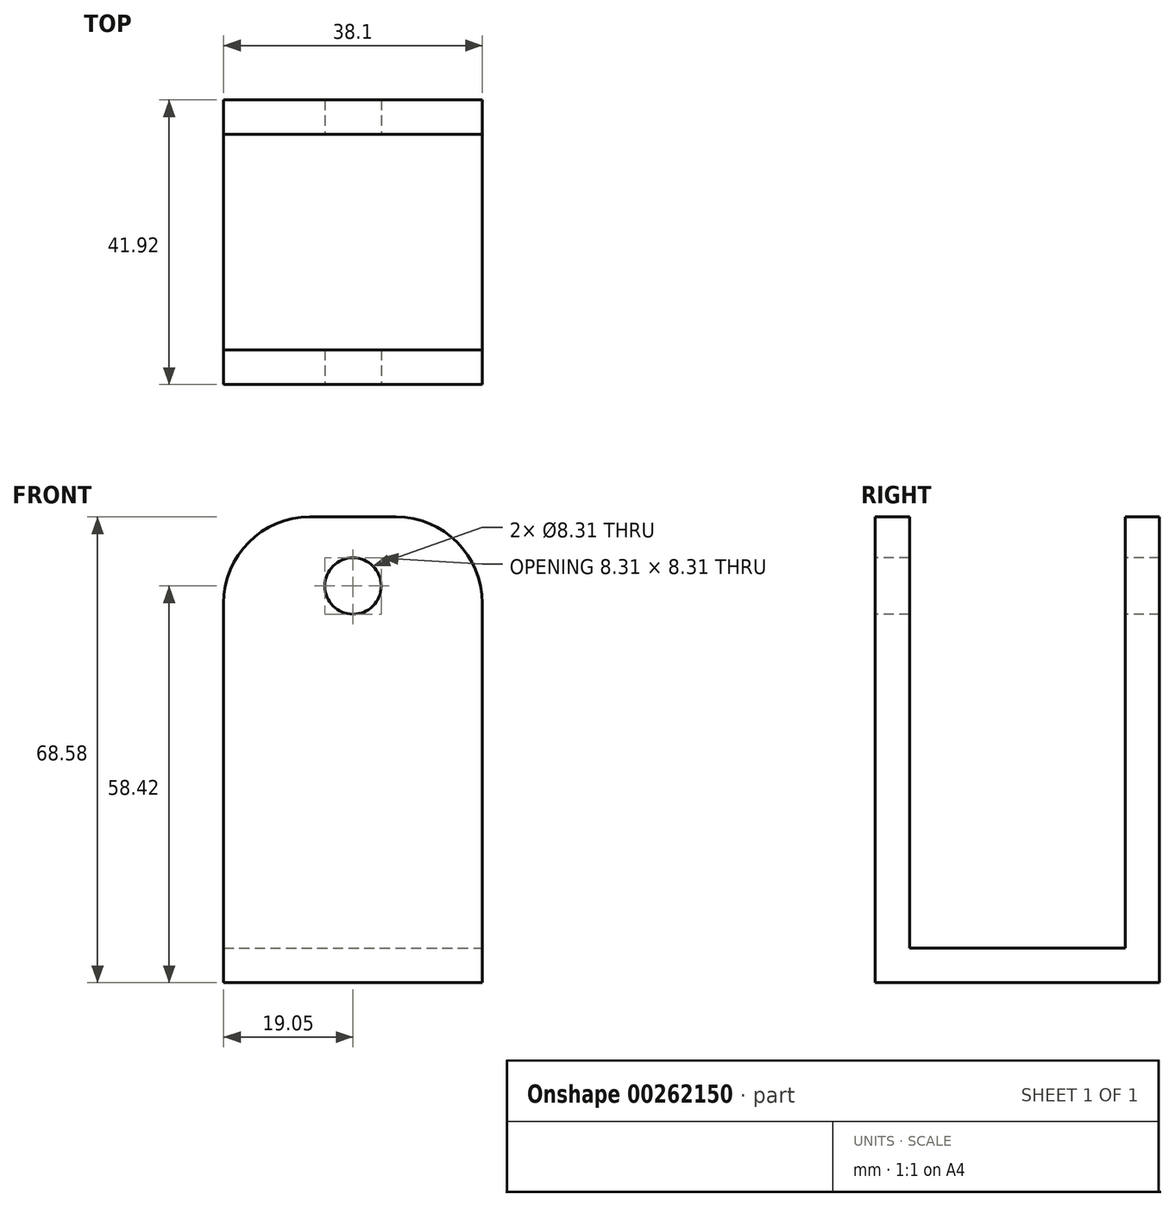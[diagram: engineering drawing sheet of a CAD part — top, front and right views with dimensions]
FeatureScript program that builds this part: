
annotation { "Feature Type Name" : "Feature", "Feature Type Description" : "" }
export const myFeature = defineFeature(function(context is Context, id is Id, definition is map)
    precondition{}
    {
        {
            var Q0;
            Q0=qCreatedBy(makeId("Top.planeOp"),FACE);
            var sketch = newSketch(context, id + "F0", { "sketchPlane" : qUnion([Q0])});
            skLineSegment(sketch, "E0.bottom", {"start": v(19.05, 20.95) * mm, "end": v(-19.05, 20.95) * mm});
            skLineSegment(sketch, "E0.top", {"start": v(19.05, -20.96) * mm, "end": v(-19.05, -20.96) * mm});
            skLineSegment(sketch, "E0.left", {"start": v(19.05, 20.95) * mm, "end": v(19.05, -20.96) * mm});
            skLineSegment(sketch, "E0.right", {"start": v(-19.05, 20.96) * mm, "end": v(-19.05, -20.96) * mm});
            skPoint(sketch, "E0.middle", {"position": v(0, 0) * mm});
            skSolve(sketch);
        }
        {
            var Q0;
            Q0=makeQuery(id+"F0.imprint","IMPRINT",FACE,{"disambiguationData":[TD([[makeQuery(id+"F0.imprint","IMPRINT",EDGE,{"derivedFrom":sQuery(id+"F0.wireOp",EDGE,"E0.bottom")}),1.0]])]});
            extrude(context, id + "F1", {"entities" : qUnion([Q0]), "depth" : 5.08 * mm});
        }
        {
            var Q0;
            Q0=makeQuery(id+"F1.opExtrude","CAP_FACE",FACE,{"disambiguationData":[OSD([sQuery(id+"F0.wireOp",EDGE,"E0.bottom"),sQuery(id+"F0.wireOp",EDGE,"E0.top"),sQuery(id+"F0.wireOp",EDGE,"E0.left"),sQuery(id+"F0.wireOp",EDGE,"E0.right")])],"isStart":false});
            var sketch = newSketch(context, id + "F2", { "sketchPlane" : qUnion([Q0])});
            skLineSegment(sketch, "E1", {"start": v(-19.05, 15.87) * mm, "end": v(19.05, 15.87) * mm});
            skLineSegment(sketch, "E2", {"start": v(-19.05, -15.88) * mm, "end": v(19.05, -15.87) * mm});
            skSolve(sketch);
        }
        {
            var Q0;
            {var subQ0=sQuery(id+"F2.wireOp",EDGE,"E1");Q0=makeQuery(id+"F2.imprint","IMPRINT",FACE,{"disambiguationData":[TD([[makeQuery(id+"F2.imprint","IMPRINT",EDGE,{"derivedFrom":subQ0}),1.0]])]});}
            var Q1;
            {var subQ0=sQuery(id+"F2.wireOp",EDGE,"E2");Q1=makeQuery(id+"F2.imprint","IMPRINT",FACE,{"disambiguationData":[TD([[makeQuery(id+"F2.imprint","IMPRINT",EDGE,{"derivedFrom":subQ0}),-1.0]])]});}
            extrude(context, id + "F3", {"entities" : qUnion([Q0, Q1]), "operationType" : NewBodyOperationType.ADD, "depth" : 63.5 * mm});
        }
        {
            var Q0;
            {var subQ0=sQuery(id+"F0.wireOp",EDGE,"E0.top");Q0=makeQuery(id+"F3.boolean.opBoolean","MERGE",FACE,{"derivedFrom":[makeQuery(id+"F1.opExtrude","SWEPT_FACE",FACE,{"disambiguationData":[OSD([subQ0])]}),makeQuery(id+"F3.opExtrude","SWEPT_FACE",FACE,{"disambiguationData":[OSD([subQ0])]})]});}
            var sketch = newSketch(context, id + "F4", { "sketchPlane" : qUnion([Q0])});
            skLineSegment(sketch, "E3", {"start": v(0, 0) * mm, "end": v(0, 68.58) * mm, "construction": true});
            skCircle(sketch, "E4", {"center": v(0, 58.42) * mm, "radius": 4.15 * mm});
            skSolve(sketch);
        }
        {
            var Q0;
            Q0=makeQuery(id+"F4.imprint","IMPRINT",FACE,{"disambiguationData":[TD([[makeQuery(id+"F4.imprint","IMPRINT",EDGE,{"derivedFrom":sQuery(id+"F4.wireOp",EDGE,"E4")}),1.0]])]});
            extrude(context, id + "F5", {"entities" : qUnion([Q0]), "operationType" : NewBodyOperationType.REMOVE, "oppositeDirection" : true, "depth" : 48.77 * mm});
        }
        {
            var Q0;
            {var subQ0=sQuery(id+"F0.wireOp",EDGE,"E0.right");var subQ1=makeQuery(id+"F1.opExtrude","CAP_EDGE",EDGE,{"disambiguationData":[OSD([subQ0])],"isStart":false});Q0=makeQuery(id+"F3.opExtrude","CAP_EDGE",EDGE,{"disambiguationData":[OSD([subQ0]),TDD([makeQuery(id+"F2.imprint","IMPRINT",EDGE,{"disambiguationData":[TD([[makeQuery(id+"F2.imprint","INTERSECT",VERTEX,{"derivedFrom":[makeQuery(id+"F1.opExtrude","CAP_EDGE",EDGE,{"disambiguationData":[OSD([sQuery(id+"F0.wireOp",EDGE,"E0.top")])],"isStart":false}),subQ1]}),1.0]])],"derivedFrom":subQ1})])],"isStart":false});}
            var Q1;
            {var subQ0=sQuery(id+"F0.wireOp",EDGE,"E0.right");var subQ1=makeQuery(id+"F1.opExtrude","CAP_EDGE",EDGE,{"disambiguationData":[OSD([subQ0])],"isStart":false});Q1=makeQuery(id+"F3.opExtrude","CAP_EDGE",EDGE,{"disambiguationData":[OSD([subQ0]),TDD([makeQuery(id+"F2.imprint","IMPRINT",EDGE,{"disambiguationData":[TD([[makeQuery(id+"F2.imprint","INTERSECT",VERTEX,{"derivedFrom":[makeQuery(id+"F1.opExtrude","CAP_EDGE",EDGE,{"disambiguationData":[OSD([sQuery(id+"F0.wireOp",EDGE,"E0.bottom")])],"isStart":false}),subQ1]}),-1.0]])],"derivedFrom":subQ1})])],"isStart":false});}
            var Q2;
            {var subQ0=sQuery(id+"F0.wireOp",EDGE,"E0.left");var subQ1=makeQuery(id+"F1.opExtrude","CAP_EDGE",EDGE,{"disambiguationData":[OSD([subQ0])],"isStart":false});Q2=makeQuery(id+"F3.opExtrude","CAP_EDGE",EDGE,{"disambiguationData":[OSD([subQ0]),TDD([makeQuery(id+"F2.imprint","IMPRINT",EDGE,{"disambiguationData":[TD([[makeQuery(id+"F2.imprint","INTERSECT",VERTEX,{"derivedFrom":[makeQuery(id+"F1.opExtrude","CAP_EDGE",EDGE,{"disambiguationData":[OSD([sQuery(id+"F0.wireOp",EDGE,"E0.top")])],"isStart":false}),subQ1]}),1.0]])],"derivedFrom":subQ1})])],"isStart":false});}
            var Q3;
            {var subQ0=sQuery(id+"F0.wireOp",EDGE,"E0.left");var subQ1=makeQuery(id+"F1.opExtrude","CAP_EDGE",EDGE,{"disambiguationData":[OSD([subQ0])],"isStart":false});Q3=makeQuery(id+"F3.opExtrude","CAP_EDGE",EDGE,{"disambiguationData":[OSD([subQ0]),TDD([makeQuery(id+"F2.imprint","IMPRINT",EDGE,{"disambiguationData":[TD([[makeQuery(id+"F2.imprint","INTERSECT",VERTEX,{"derivedFrom":[makeQuery(id+"F1.opExtrude","CAP_EDGE",EDGE,{"disambiguationData":[OSD([sQuery(id+"F0.wireOp",EDGE,"E0.bottom")])],"isStart":false}),subQ1]}),-1.0]])],"derivedFrom":subQ1})])],"isStart":false});}
            fillet(context, id + "F6", {"entities" : qUnion([Q0, Q1, Q2, Q3]), "radius" : 12.7 * mm, "tangentPropagation" : true, "allowEdgeOverflow" : false});
        }
    });
